annotation { "Feature Type Name" : "Feature", "Feature Type Description" : "" }
export const myFeature = defineFeature(function(context is Context, id is Id, definition is map)
    precondition{}
    {
        {
            var Q0;
            Q0=qCreatedBy(makeId("Front.planeOp"),FACE);
            var sketch = newSketch(context, id + "F0", { "sketchPlane" : qUnion([Q0])});
            skLineSegment(sketch, "E0.bottom", {"start": v(-150, 150) * mm, "end": v(150, 150) * mm});
            skLineSegment(sketch, "E0.top", {"start": v(-150, -150) * mm, "end": v(150, -150) * mm});
            skLineSegment(sketch, "E0.left", {"start": v(-150, 150) * mm, "end": v(-150, -150) * mm});
            skLineSegment(sketch, "E0.right", {"start": v(150, 150) * mm, "end": v(150, -150) * mm});
            skPoint(sketch, "E0.middle", {"position": v(0, 0) * mm});
            skSolve(sketch);
        }
        {
            var Q0;
            Q0 = qSketchRegion(id + "F0", true);
            extrude(context, id + "F1", {"entities" : qUnion([Q0]), "oppositeDirection" : true, "depth" : 2 * mm});
        }
        {
            var Q0;
            Q0=makeQuery(id+"F1.opExtrude","CAP_FACE",FACE,{"disambiguationData":[OSD([sQuery(id+"F0.wireOp",EDGE,"E0.bottom"),sQuery(id+"F0.wireOp",EDGE,"E0.top"),sQuery(id+"F0.wireOp",EDGE,"E0.left"),sQuery(id+"F0.wireOp",EDGE,"E0.right")])],"isStart":true});
            var sketch = newSketch(context, id + "F2", { "sketchPlane" : qUnion([Q0])});
            skLineSegment(sketch, "E1.bottom", {"start": v(91.5, -117) * mm, "end": v(48.5, -117) * mm, "construction": true});
            skLineSegment(sketch, "E1.top", {"start": v(91.5, -23) * mm, "end": v(48.5, -23) * mm, "construction": true});
            skLineSegment(sketch, "E1.left", {"start": v(91.5, -117) * mm, "end": v(91.5, -23) * mm, "construction": true});
            skLineSegment(sketch, "E1.right", {"start": v(48.5, -117) * mm, "end": v(48.5, -23) * mm, "construction": true});
            skPoint(sketch, "E1.middle", {"position": v(70, -70) * mm});
            skCircle(sketch, "E2", {"center": v(48.5, -23) * mm, "radius": 1.5 * mm});
            skCircle(sketch, "E3", {"center": v(91.5, -23) * mm, "radius": 1.5 * mm});
            skCircle(sketch, "E4", {"center": v(48.5, -117) * mm, "radius": 1.5 * mm});
            skCircle(sketch, "E5", {"center": v(91.5, -117) * mm, "radius": 1.5 * mm});
            skSolve(sketch);
        }
        {
            var Q0;
            Q0 = qSketchRegion(id + "F2", true);
            var Q1;
            Q1=makeQuery(id+"F1.opExtrude","CAP_FACE",FACE,{"disambiguationData":[OSD([sQuery(id+"F0.wireOp",EDGE,"E0.bottom"),sQuery(id+"F0.wireOp",EDGE,"E0.top"),sQuery(id+"F0.wireOp",EDGE,"E0.left"),sQuery(id+"F0.wireOp",EDGE,"E0.right")])],"isStart":false});
            extrude(context, id + "F3", {"entities" : qUnion([Q0]), "operationType" : NewBodyOperationType.REMOVE, "endBound" : BoundingType.UP_TO_SURFACE, "oppositeDirection" : true, "endBoundEntityFace" : qUnion([Q1]), "depth" : 25 * mm});
        }
        {
            var Q0;
            Q0=makeQuery(id+"F1.opExtrude","CAP_FACE",FACE,{"disambiguationData":[OSD([sQuery(id+"F0.wireOp",EDGE,"E0.bottom"),sQuery(id+"F0.wireOp",EDGE,"E0.top"),sQuery(id+"F0.wireOp",EDGE,"E0.left"),sQuery(id+"F0.wireOp",EDGE,"E0.right")])],"isStart":true});
            var sketch = newSketch(context, id + "F4", { "sketchPlane" : qUnion([Q0])});
            skLineSegment(sketch, "E6.bottom", {"start": v(-69, 40.08) * mm, "end": v(-111, 40.08) * mm, "construction": true});
            skLineSegment(sketch, "E6.top", {"start": v(-69, 82.08) * mm, "end": v(-111, 82.08) * mm, "construction": true});
            skLineSegment(sketch, "E6.left", {"start": v(-69, 40.08) * mm, "end": v(-69, 82.08) * mm, "construction": true});
            skLineSegment(sketch, "E6.right", {"start": v(-111, 40.08) * mm, "end": v(-111, 82.08) * mm, "construction": true});
            skPoint(sketch, "E6.middle", {"position": v(-90, 61.08) * mm});
            skCircle(sketch, "E7", {"center": v(-111, 82.08) * mm, "radius": 1.5 * mm});
            skCircle(sketch, "E8", {"center": v(-69, 82.08) * mm, "radius": 1.5 * mm});
            skCircle(sketch, "E9", {"center": v(-69, 40.08) * mm, "radius": 1.5 * mm});
            skCircle(sketch, "E10", {"center": v(-111, 40.08) * mm, "radius": 1.5 * mm});
            skSolve(sketch);
        }
        {
            var Q0;
            Q0 = qSketchRegion(id + "F4", true);
            var Q1;
            Q1=makeQuery(id+"F1.opExtrude","CAP_FACE",FACE,{"disambiguationData":[OSD([sQuery(id+"F0.wireOp",EDGE,"E0.bottom"),sQuery(id+"F0.wireOp",EDGE,"E0.top"),sQuery(id+"F0.wireOp",EDGE,"E0.left"),sQuery(id+"F0.wireOp",EDGE,"E0.right")])],"isStart":false});
            extrude(context, id + "F5", {"entities" : qUnion([Q0]), "operationType" : NewBodyOperationType.REMOVE, "endBound" : BoundingType.UP_TO_SURFACE, "oppositeDirection" : true, "endBoundEntityFace" : qUnion([Q1]), "depth" : 25 * mm});
        }
        {
            var Q0;
            Q0=makeQuery(id+"F1.opExtrude","CAP_FACE",FACE,{"disambiguationData":[OSD([sQuery(id+"F0.wireOp",EDGE,"E0.bottom"),sQuery(id+"F0.wireOp",EDGE,"E0.top"),sQuery(id+"F0.wireOp",EDGE,"E0.left"),sQuery(id+"F0.wireOp",EDGE,"E0.right")])],"isStart":true});
            var sketch = newSketch(context, id + "F6", { "sketchPlane" : qUnion([Q0])});
            skText(sketch, "E11", { "text": "Power Supply", "fontName": "OpenSans-Bold.ttf"});
            skText(sketch, "E12", { "text": "Main Board", "fontName": "OpenSans-Bold.ttf"});
            const initialGuessF6  = {"E11": [-0.14882, 0.0559, 1, 0, 0.01634], "E12": [-0.03242, -0.07581, 1, 0, 0.02195]};
            skSetInitialGuess(sketch, initialGuessF6);
            skSolve(sketch);
        }
        {
            var Q0;
            Q0 = qSketchRegion(id + "F6", true);
            extrude(context, id + "F7", {"entities" : qUnion([Q0]), "operationType" : NewBodyOperationType.REMOVE, "oppositeDirection" : true, "depth" : .5 * mm});
        }
    });